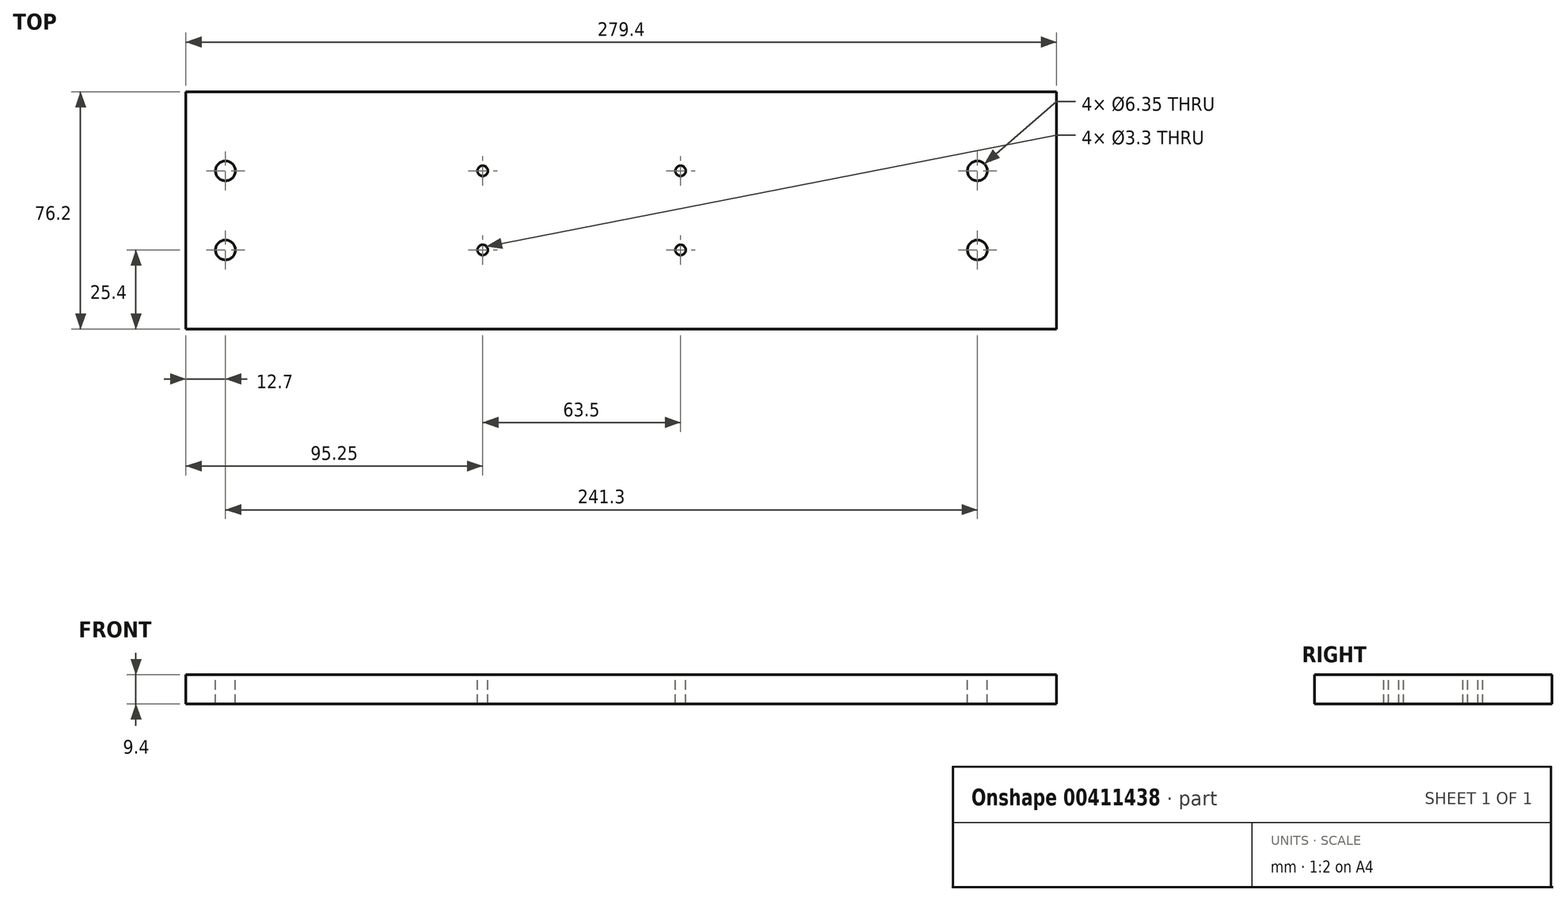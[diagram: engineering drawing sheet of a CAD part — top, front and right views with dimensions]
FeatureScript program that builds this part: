
annotation { "Feature Type Name" : "Feature", "Feature Type Description" : "" }
export const myFeature = defineFeature(function(context is Context, id is Id, definition is map)
    precondition{}
    {
        {
            var Q0;
            Q0=qCreatedBy(makeId("Top.planeOp"),FACE);
            var sketch = newSketch(context, id + "F0", { "sketchPlane" : qUnion([Q0])});
            skLineSegment(sketch, "E0.bottom", {"start": v(-139.7, 38.1) * mm, "end": v(139.7, 38.1) * mm});
            skLineSegment(sketch, "E0.top", {"start": v(-139.7, -38.1) * mm, "end": v(139.7, -38.1) * mm});
            skLineSegment(sketch, "E0.left", {"start": v(-139.7, 38.1) * mm, "end": v(-139.7, -38.1) * mm});
            skLineSegment(sketch, "E0.right", {"start": v(139.7, 38.1) * mm, "end": v(139.7, -38.1) * mm});
            skSolve(sketch);
        }
        {
            var Q0;
            Q0=qSketchRegion(id+"F0",true);
            extrude(context, id + "F1", {"entities" : qUnion([Q0]), "depth" : 9.4 * mm});
        }
        {
            var Q0;
            Q0=makeQuery(id+"F1.opExtrude","CAP_FACE",FACE,{"disambiguationData":[OSD([sQuery(id+"F0.wireOp",EDGE,"E0.bottom"),sQuery(id+"F0.wireOp",EDGE,"E0.top"),sQuery(id+"F0.wireOp",EDGE,"E0.left"),sQuery(id+"F0.wireOp",EDGE,"E0.right")])],"isStart":false});
            var sketch = newSketch(context, id + "F2", { "sketchPlane" : qUnion([Q0])});
            skCircle(sketch, "E1", {"center": v(-127, 12.7) * mm, "radius": 3.18 * mm});
            skCircle(sketch, "E2", {"center": v(-127, -12.7) * mm, "radius": 3.18 * mm});
            skCircle(sketch, "E3", {"center": v(114.3, 12.7) * mm, "radius": 3.18 * mm});
            skCircle(sketch, "E4", {"center": v(114.3, -12.7) * mm, "radius": 3.18 * mm});
            skCircle(sketch, "E5", {"center": v(-44.45, 12.7) * mm, "radius": 1.65 * mm});
            skCircle(sketch, "E6", {"center": v(-44.45, -12.7) * mm, "radius": 1.65 * mm});
            skCircle(sketch, "E7", {"center": v(19.05, 12.7) * mm, "radius": 1.65 * mm});
            skCircle(sketch, "E8", {"center": v(19.05, -12.7) * mm, "radius": 1.65 * mm});
            skSolve(sketch);
        }
        {
            var Q0;
            Q0=makeQuery(id+"F2.imprint","IMPRINT",FACE,{"disambiguationData":[TD([[makeQuery(id+"F2.imprint","IMPRINT",EDGE,{"derivedFrom":sQuery(id+"F2.wireOp",EDGE,"E1")}),-1.0]])]});
            var Q1;
            Q1=sQuery(id+"F2.wireOp",EDGE,"E1");
            var Q2;
            Q2=sQuery(id+"F2.wireOp",EDGE,"E2");
            var Q3;
            Q3=sQuery(id+"F2.wireOp",EDGE,"E5");
            var Q4;
            Q4=sQuery(id+"F2.wireOp",EDGE,"E6");
            var Q5;
            Q5=sQuery(id+"F2.wireOp",EDGE,"E8");
            var Q6;
            Q6=sQuery(id+"F2.wireOp",EDGE,"E7");
            var Q7;
            Q7=sQuery(id+"F2.wireOp",EDGE,"E3");
            var Q8;
            Q8=sQuery(id+"F2.wireOp",EDGE,"E4");
            extrude(context, id + "F3", {"entities" : qUnion([Q0]), "operationType" : NewBodyOperationType.INTERSECT, "surfaceEntities" : qUnion([Q1, Q2, Q3, Q4, Q5, Q6, Q7, Q8]), "endBound" : BoundingType.SYMMETRIC, "oppositeDirection" : true, "depth" : 25.4 * mm});
        }
    });
